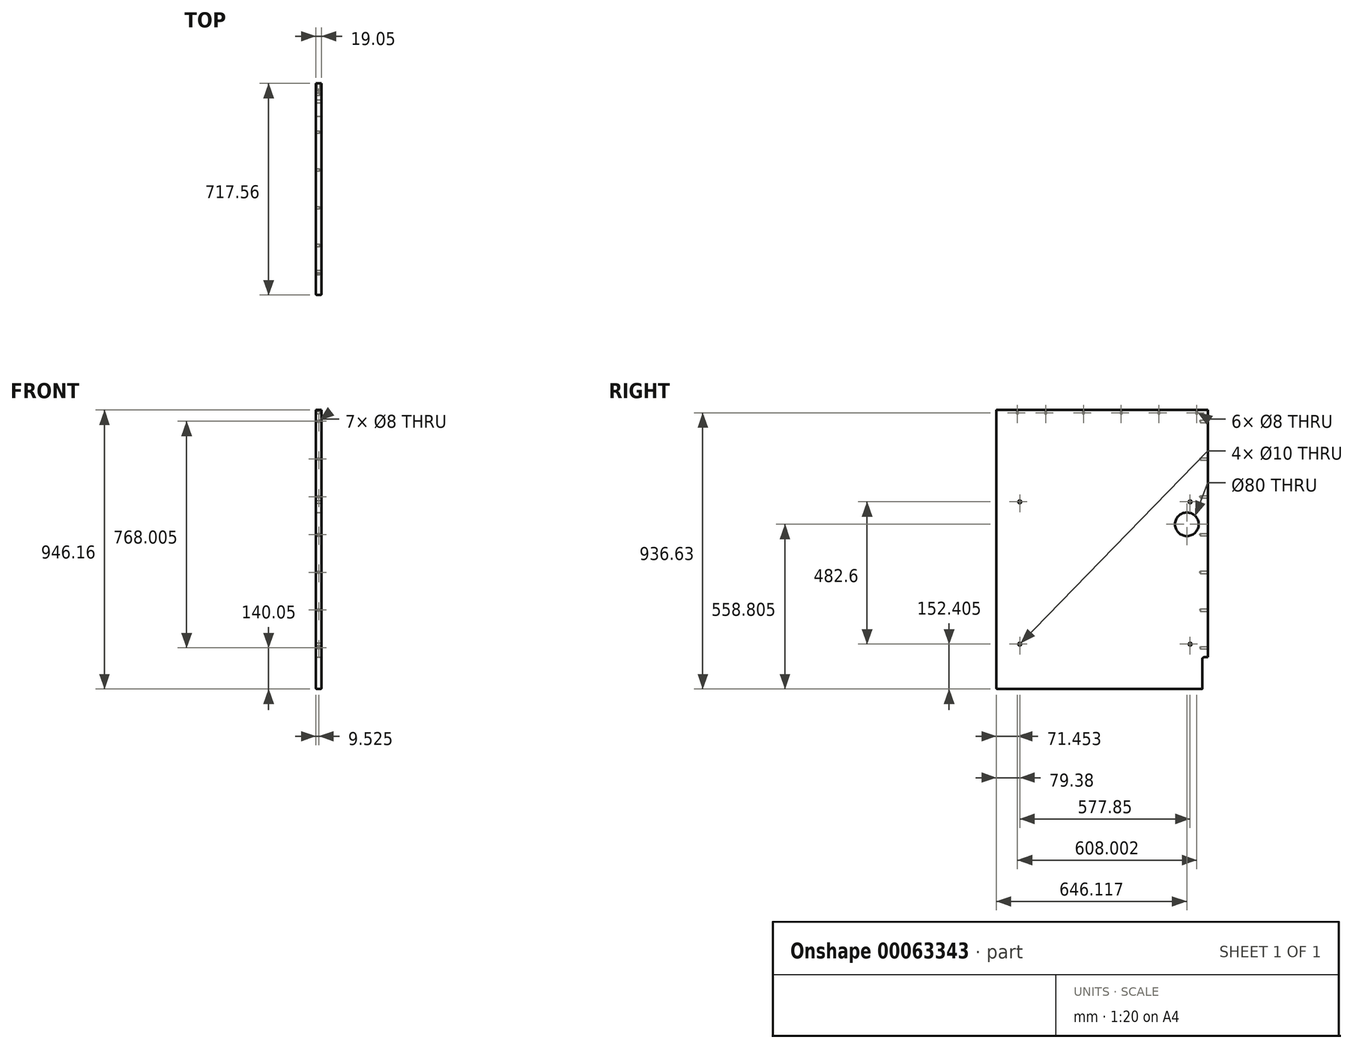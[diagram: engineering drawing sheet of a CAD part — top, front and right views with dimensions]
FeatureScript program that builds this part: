
annotation { "Feature Type Name" : "Feature", "Feature Type Description" : "" }
export const myFeature = defineFeature(function(context is Context, id is Id, definition is map)
    precondition{}
    {
        {
            var Q0;
            Q0=qCreatedBy(makeId("Right.planeOp"),FACE);
            var sketch = newSketch(context, id + "F0", { "sketchPlane" : qUnion([Q0])});
            skLineSegment(sketch, "E0.rect.bottom", {"start": v(358.78, -473.08) * mm, "end": v(-358.78, -473.08) * mm});
            skLineSegment(sketch, "E0.rect.top", {"start": v(358.78, 473.08) * mm, "end": v(-358.77, 473.07) * mm});
            skLineSegment(sketch, "E0.rect.left", {"start": v(358.78, -473.08) * mm, "end": v(358.78, 473.08) * mm});
            skLineSegment(sketch, "E0.rect.right", {"start": v(-358.78, -473.08) * mm, "end": v(-358.77, 473.08) * mm});
            skPoint(sketch, "E0.rect.middle", {"position": v(0, 0) * mm});
            skSolve(sketch);
        }
        {
            var Q0;
            Q0=makeQuery(id+"F0.imprint","IMPRINT",FACE,{"disambiguationData":[TD([[makeQuery(id+"F0.imprint","IMPRINT",EDGE,{"derivedFrom":sQuery(id+"F0.wireOp",EDGE,"E0.rect.bottom")}),-1.0]])]});
            extrude(context, id + "F1", {"entities" : qUnion([Q0]), "oppositeDirection" : true, "depth" : 19.05 * mm});
        }
        {
            var Q0;
            Q0=makeQuery(id+"F1.opExtrude","CAP_FACE",FACE,{"disambiguationData":[OSD([sQuery(id+"F0.wireOp",EDGE,"E0.rect.bottom"),sQuery(id+"F0.wireOp",EDGE,"E0.rect.top"),sQuery(id+"F0.wireOp",EDGE,"E0.rect.left"),sQuery(id+"F0.wireOp",EDGE,"E0.rect.right")])],"isStart":false});
            var sketch = newSketch(context, id + "F2", { "sketchPlane" : qUnion([Q0])});
            skPoint(sketch, "E1", {"position": v(-320.68, 463.55) * mm});
            skPoint(sketch, "E2", {"position": v(-192.67, 463.55) * mm});
            skPoint(sketch, "E3", {"position": v(-64.67, 463.55) * mm});
            skPoint(sketch, "E4", {"position": v(63.33, 463.55) * mm});
            skPoint(sketch, "E5", {"position": v(191.33, 463.55) * mm});
            skPoint(sketch, "E6", {"position": v(287.33, 463.55) * mm});
            skSolve(sketch);
        }
        {
            var Q0;
            Q0=sQuery(id+"F2.wireOp",VERTEX,"E1");
            var Q1;
            Q1=sQuery(id+"F2.wireOp",VERTEX,"E2");
            var Q2;
            Q2=sQuery(id+"F2.wireOp",VERTEX,"E3");
            var Q3;
            Q3=sQuery(id+"F2.wireOp",VERTEX,"E4");
            var Q4;
            Q4=sQuery(id+"F2.wireOp",VERTEX,"E5");
            var Q5;
            Q5=sQuery(id+"F2.wireOp",VERTEX,"E6");
            var Q6;
            Q6=makeQuery(id+"F1.opExtrude","SWEPT_BODY",BODY,{"disambiguationData":[OSD([sQuery(id+"F0.wireOp",EDGE,"E0.rect.bottom"),sQuery(id+"F0.wireOp",EDGE,"E0.rect.top"),sQuery(id+"F0.wireOp",EDGE,"E0.rect.left"),sQuery(id+"F0.wireOp",EDGE,"E0.rect.right")])]});
            hole(context, id + "F3", {"style" : HoleStyle.SIMPLE, "holeDiameter" : 8 * mm, "endStyle" : HoleEndStyle.BLIND, "holeDepth" : 12.7 * mm, "locations" : qUnion([Q0, Q1, Q2, Q3, Q4, Q5]), "scope" : qUnion([Q6])});
        }
        {
            var Q0;
            Q0=makeQuery(id+"F1.opExtrude","CAP_FACE",FACE,{"disambiguationData":[OSD([sQuery(id+"F0.wireOp",EDGE,"E0.rect.bottom"),sQuery(id+"F0.wireOp",EDGE,"E0.rect.top"),sQuery(id+"F0.wireOp",EDGE,"E0.rect.left"),sQuery(id+"F0.wireOp",EDGE,"E0.rect.right")])],"isStart":true});
            var sketch = newSketch(context, id + "F4", { "sketchPlane" : qUnion([Q0])});
            skLineSegment(sketch, "E7.bottom", {"start": v(358.78, -473.08) * mm, "end": v(339.73, -473.08) * mm});
            skLineSegment(sketch, "E7.top", {"start": v(358.78, -365.13) * mm, "end": v(346.08, -365.13) * mm});
            skLineSegment(sketch, "E7.left", {"start": v(358.78, -473.08) * mm, "end": v(358.78, -365.13) * mm});
            skLineSegment(sketch, "E7.right", {"start": v(339.73, -473.08) * mm, "end": v(339.73, -371.48) * mm});
            skPoint(sketch, "E8.visualSharp", {"position": v(339.73, -365.13) * mm});
            skArc(sketch, "E8.filletArc", {"start": v(346.08, -365.13) * mm, "mid": v(341.58, -366.98) * mm, "end": v(339.73, -371.48) * mm});
            skSolve(sketch);
        }
        {
            var Q0;
            Q0=makeQuery(id+"F4.imprint","IMPRINT",FACE,{"disambiguationData":[TD([[makeQuery(id+"F4.imprint","IMPRINT",EDGE,{"derivedFrom":sQuery(id+"F4.wireOp",EDGE,"E7.bottom")}),-1.0]])]});
            extrude(context, id + "F5", {"entities" : qUnion([Q0]), "operationType" : NewBodyOperationType.REMOVE, "endBound" : BoundingType.THROUGH_ALL, "oppositeDirection" : true, "depth" : 25.4 * mm});
        }
        {
            var Q0;
            Q0=makeQuery(id+"F1.opExtrude","CAP_FACE",FACE,{"disambiguationData":[OSD([sQuery(id+"F0.wireOp",EDGE,"E0.rect.bottom"),sQuery(id+"F0.wireOp",EDGE,"E0.rect.top"),sQuery(id+"F0.wireOp",EDGE,"E0.rect.left"),sQuery(id+"F0.wireOp",EDGE,"E0.rect.right")])],"isStart":true});
            var sketch = newSketch(context, id + "F6", { "sketchPlane" : qUnion([Q0])});
            skPoint(sketch, "E9", {"position": v(-279.4, 161.92) * mm});
            skPoint(sketch, "E10", {"position": v(298.45, 161.92) * mm});
            skPoint(sketch, "E11", {"position": v(298.45, -320.68) * mm});
            skPoint(sketch, "E12", {"position": v(-279.4, -320.68) * mm});
            skSolve(sketch);
        }
        {
            var Q0;
            Q0=sQuery(id+"F6.wireOp",VERTEX,"E9");
            var Q1;
            Q1=sQuery(id+"F6.wireOp",VERTEX,"E12");
            var Q2;
            Q2=sQuery(id+"F6.wireOp",VERTEX,"E11");
            var Q3;
            Q3=sQuery(id+"F6.wireOp",VERTEX,"E10");
            var Q4;
            Q4=makeQuery(id+"F1.opExtrude","SWEPT_BODY",BODY,{"disambiguationData":[OSD([sQuery(id+"F0.wireOp",EDGE,"E0.rect.bottom"),sQuery(id+"F0.wireOp",EDGE,"E0.rect.top"),sQuery(id+"F0.wireOp",EDGE,"E0.rect.left"),sQuery(id+"F0.wireOp",EDGE,"E0.rect.right")])]});
            hole(context, id + "F7", {"style" : HoleStyle.SIMPLE, "holeDiameter" : 10 * mm, "endStyle" : HoleEndStyle.THROUGH, "locations" : qUnion([Q0, Q1, Q2, Q3]), "scope" : qUnion([Q4])});
        }
        {
            var Q0;
            Q0=makeQuery(id+"F1.opExtrude","CAP_FACE",FACE,{"disambiguationData":[OSD([sQuery(id+"F0.wireOp",EDGE,"E0.rect.bottom"),sQuery(id+"F0.wireOp",EDGE,"E0.rect.top"),sQuery(id+"F0.wireOp",EDGE,"E0.rect.left"),sQuery(id+"F0.wireOp",EDGE,"E0.rect.right")])],"isStart":true});
            var sketch = newSketch(context, id + "F8", { "sketchPlane" : qUnion([Q0])});
            skPoint(sketch, "E13", {"position": v(287.34, 85.72) * mm});
            skSolve(sketch);
        }
        {
            var Q0;
            Q0=sQuery(id+"F8.wireOp",VERTEX,"E13");
            var Q1;
            Q1=makeQuery(id+"F1.opExtrude","SWEPT_BODY",BODY,{"disambiguationData":[OSD([sQuery(id+"F0.wireOp",EDGE,"E0.rect.bottom"),sQuery(id+"F0.wireOp",EDGE,"E0.rect.top"),sQuery(id+"F0.wireOp",EDGE,"E0.rect.left"),sQuery(id+"F0.wireOp",EDGE,"E0.rect.right")])]});
            hole(context, id + "F9", {"style" : HoleStyle.SIMPLE, "holeDiameter" : 80 * mm, "endStyle" : HoleEndStyle.THROUGH, "locations" : qUnion([Q0]), "scope" : qUnion([Q1])});
        }
        {
            var Q0;
            Q0=makeQuery(id+"F1.opExtrude","SWEPT_FACE",FACE,{"disambiguationData":[OSD([sQuery(id+"F0.wireOp",EDGE,"E0.rect.left")])]});
            var sketch = newSketch(context, id + "F10", { "sketchPlane" : qUnion([Q0])});
            skPoint(sketch, "E14", {"position": v(9.53, 434.98) * mm});
            skPoint(sketch, "E15", {"position": v(9.53, 306.97) * mm});
            skPoint(sketch, "E16", {"position": v(9.53, 178.97) * mm});
            skPoint(sketch, "E17", {"position": v(9.53, 50.97) * mm});
            skPoint(sketch, "E18", {"position": v(9.53, -77.03) * mm});
            skPoint(sketch, "E19", {"position": v(9.53, -205.03) * mm});
            skPoint(sketch, "E20", {"position": v(9.53, -333.03) * mm});
            skSolve(sketch);
        }
        {
            var Q0;
            Q0=sQuery(id+"F10.wireOp",VERTEX,"E14");
            var Q1;
            Q1=sQuery(id+"F10.wireOp",VERTEX,"E15");
            var Q2;
            Q2=sQuery(id+"F10.wireOp",VERTEX,"E16");
            var Q3;
            Q3=sQuery(id+"F10.wireOp",VERTEX,"E17");
            var Q4;
            Q4=sQuery(id+"F10.wireOp",VERTEX,"E18");
            var Q5;
            Q5=sQuery(id+"F10.wireOp",VERTEX,"E19");
            var Q6;
            Q6=sQuery(id+"F10.wireOp",VERTEX,"E20");
            var Q7;
            Q7=makeQuery(id+"F1.opExtrude","SWEPT_BODY",BODY,{"disambiguationData":[OSD([sQuery(id+"F0.wireOp",EDGE,"E0.rect.bottom"),sQuery(id+"F0.wireOp",EDGE,"E0.rect.top"),sQuery(id+"F0.wireOp",EDGE,"E0.rect.left"),sQuery(id+"F0.wireOp",EDGE,"E0.rect.right")])]});
            hole(context, id + "F11", {"style" : HoleStyle.SIMPLE, "holeDiameter" : 8 * mm, "endStyle" : HoleEndStyle.BLIND, "holeDepth" : 25.4 * mm, "locations" : qUnion([Q0, Q1, Q2, Q3, Q4, Q5, Q6]), "scope" : qUnion([Q7])});
        }
        {
            var Q0;
            Q0=makeQuery(id+"F1.opExtrude","CAP_EDGE",EDGE,{"disambiguationData":[OSD([sQuery(id+"F0.wireOp",EDGE,"E0.rect.right")])],"isStart":false});
            var Q1;
            Q1=makeQuery(id+"F1.opExtrude","CAP_EDGE",EDGE,{"disambiguationData":[OSD([sQuery(id+"F0.wireOp",EDGE,"E0.rect.right")])],"isStart":true});
            var Q2;
            Q2=makeQuery(id+"F1.opExtrude","CAP_EDGE",EDGE,{"disambiguationData":[OSD([sQuery(id+"F0.wireOp",EDGE,"E0.rect.bottom")])],"isStart":true});
            var Q3;
            Q3=makeQuery(id+"F1.opExtrude","CAP_EDGE",EDGE,{"disambiguationData":[OSD([sQuery(id+"F0.wireOp",EDGE,"E0.rect.bottom")])],"isStart":false});
            var Q4;
            Q4=makeQuery(id+"F1.opExtrude","SWEPT_EDGE",EDGE,{"disambiguationData":[OSD([sQuery(id+"F0.wireOp",EDGE,"E0.rect.bottom"),sQuery(id+"F0.wireOp",EDGE,"E0.rect.right")])]});
            fillet(context, id + "F12", {"entities" : qUnion([Q0, Q1, Q2, Q3, Q4]), "radius" : 3.17 * mm, "tangentPropagation" : true, "allowEdgeOverflow" : false});
        }
    });
